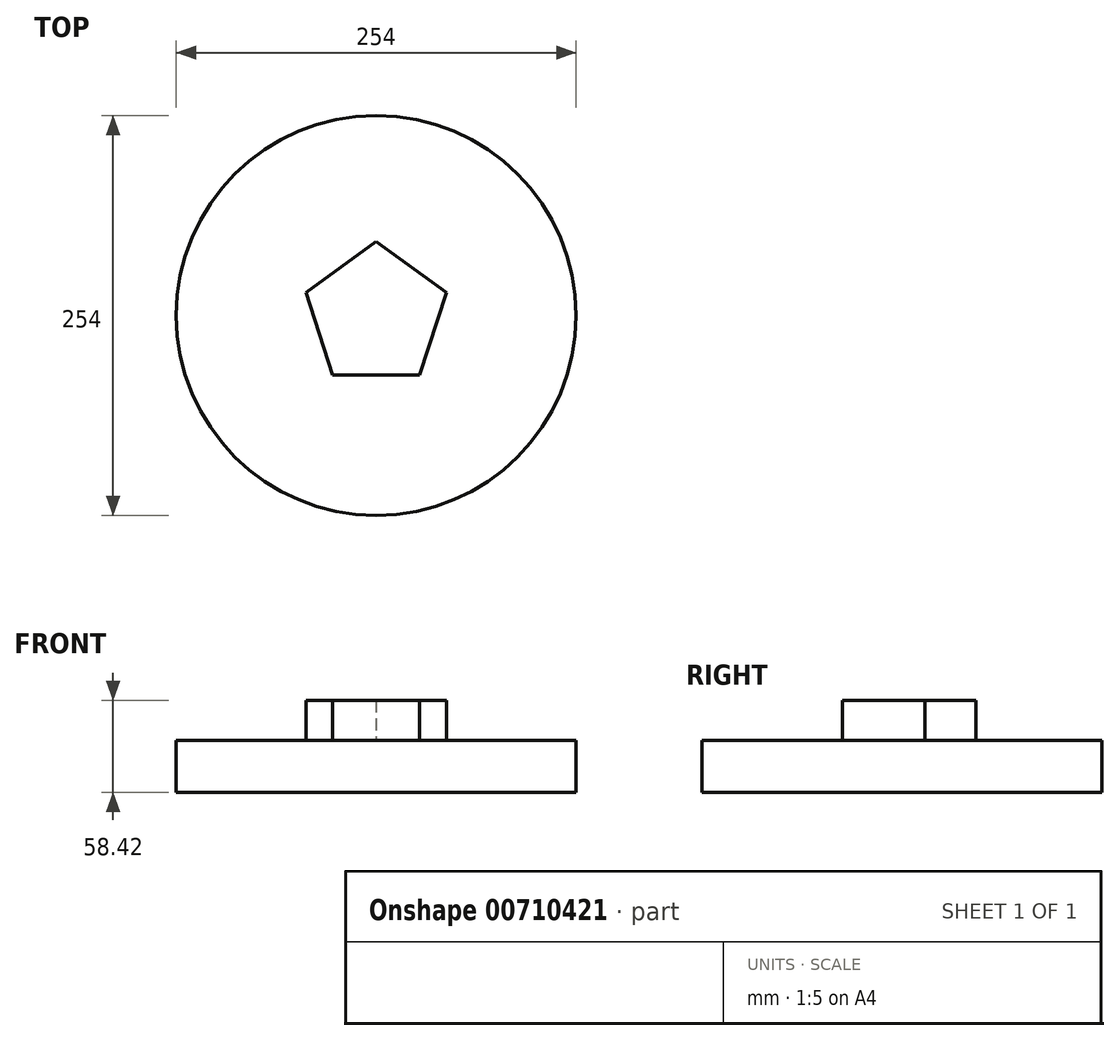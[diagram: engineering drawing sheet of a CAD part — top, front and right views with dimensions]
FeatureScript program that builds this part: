
annotation { "Feature Type Name" : "Feature", "Feature Type Description" : "" }
export const myFeature = defineFeature(function(context is Context, id is Id, definition is map)
    precondition{}
    {
        {
            var Q0;
            Q0=qCreatedBy(makeId("Top.planeOp"),FACE);
            var sketch = newSketch(context, id + "F0", { "sketchPlane" : qUnion([Q0])});
            skCircle(sketch, "E0", {"center": v(0, 0) * mm, "radius": 127 * mm});
            skSolve(sketch);
        }
        {
            var Q0;
            Q0=makeQuery(id+"F0.imprint","IMPRINT",FACE,{"disambiguationData":[TD([[makeQuery(id+"F0.imprint","IMPRINT",EDGE,{"derivedFrom":sQuery(id+"F0.wireOp",EDGE,"E0")}),1.0]])]});
            extrude(context, id + "F1", {"entities" : qUnion([Q0]), "depth" : 33.02 * mm, "offsetDistance" : 25.4 * mm});
        }
        {
            var Q0;
            Q0=makeQuery(id+"F1.opExtrude","CAP_FACE",FACE,{"disambiguationData":[OSD([sQuery(id+"F0.wireOp",EDGE,"E0")])],"isStart":false});
            var sketch = newSketch(context, id + "F2", { "sketchPlane" : qUnion([Q0])});
            skCircle(sketch, "E1.cCircle", {"center": v(0, 0) * mm, "radius": 37.9 * mm, "construction": true});
            skLineSegment(sketch, "E1.0", {"start": v(-44.53, 14.5) * mm, "end": v(0.03, 46.84) * mm});
            skLineSegment(sketch, "E1.1", {"start": v(0.03, 46.84) * mm, "end": v(44.55, 14.44) * mm});
            skLineSegment(sketch, "E1.2", {"start": v(44.55, 14.44) * mm, "end": v(27.5, -37.9) * mm});
            skLineSegment(sketch, "E1.3", {"start": v(27.5, -37.9) * mm, "end": v(-27.56, -37.87) * mm});
            skLineSegment(sketch, "E1.4", {"start": v(-27.56, -37.87) * mm, "end": v(-44.53, 14.5) * mm});
            skPoint(sketch, "E1.0.midPoint", {"position": v(-22.25, 30.67) * mm});
            skSolve(sketch);
        }
        {
            var Q0;
            Q0=makeQuery(id+"F2.imprint","IMPRINT",FACE,{"disambiguationData":[TD([[makeQuery(id+"F2.imprint","IMPRINT",EDGE,{"derivedFrom":sQuery(id+"F2.wireOp",EDGE,"E1.0")}),-1.0]])]});
            extrude(context, id + "F3", {"entities" : qUnion([Q0]), "operationType" : NewBodyOperationType.ADD, "depth" : 25.4 * mm, "offsetDistance" : 25.4 * mm});
        }
    });
